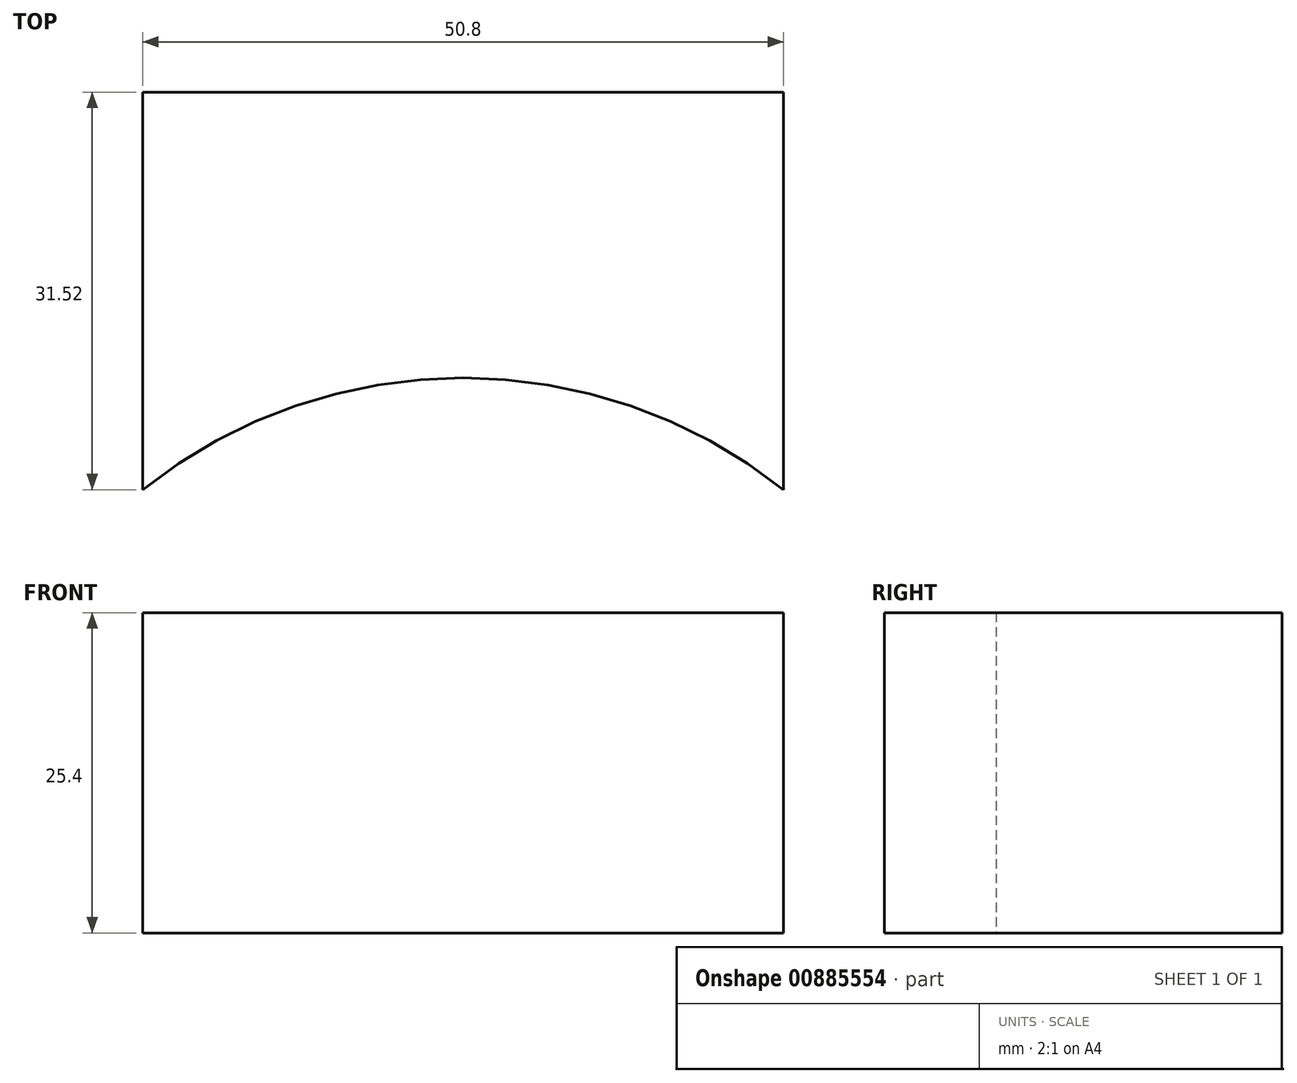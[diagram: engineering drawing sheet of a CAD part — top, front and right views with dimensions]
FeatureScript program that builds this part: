
annotation { "Feature Type Name" : "Feature", "Feature Type Description" : "" }
export const myFeature = defineFeature(function(context is Context, id is Id, definition is map)
    precondition{}
    {
        {
            var Q0;
            Q0=qCreatedBy(makeId("Top.planeOp"),FACE);
            var sketch = newSketch(context, id + "F0", { "sketchPlane" : qUnion([Q0])});
            skLineSegment(sketch, "E0.top", {"start": v(25.4, 15.76) * mm, "end": v(-25.4, 15.76) * mm});
            skLineSegment(sketch, "E0.left", {"start": v(25.4, -15.76) * mm, "end": v(25.4, 15.76) * mm});
            skLineSegment(sketch, "E0.right", {"start": v(-25.4, -15.76) * mm, "end": v(-25.4, 15.76) * mm});
            skPoint(sketch, "E0.middle", {"position": v(0, 0) * mm});
            skArc(sketch, "E1", {"start": v(25.4, -15.76) * mm, "mid": v(0, -6.9) * mm, "end": v(-25.4, -15.76) * mm});
            skSolve(sketch);
        }
        {
            var Q0;
            Q0=makeQuery(id+"F0.imprint","IMPRINT",FACE,{"disambiguationData":[TD([[makeQuery(id+"F0.imprint","IMPRINT",EDGE,{"derivedFrom":sQuery(id+"F0.wireOp",EDGE,"E0.top")}),1.0]])]});
            extrude(context, id + "F1", {"entities" : qUnion([Q0]), "depth" : 25.4 * mm, "offsetDistance" : 25.4 * mm});
        }
    });
